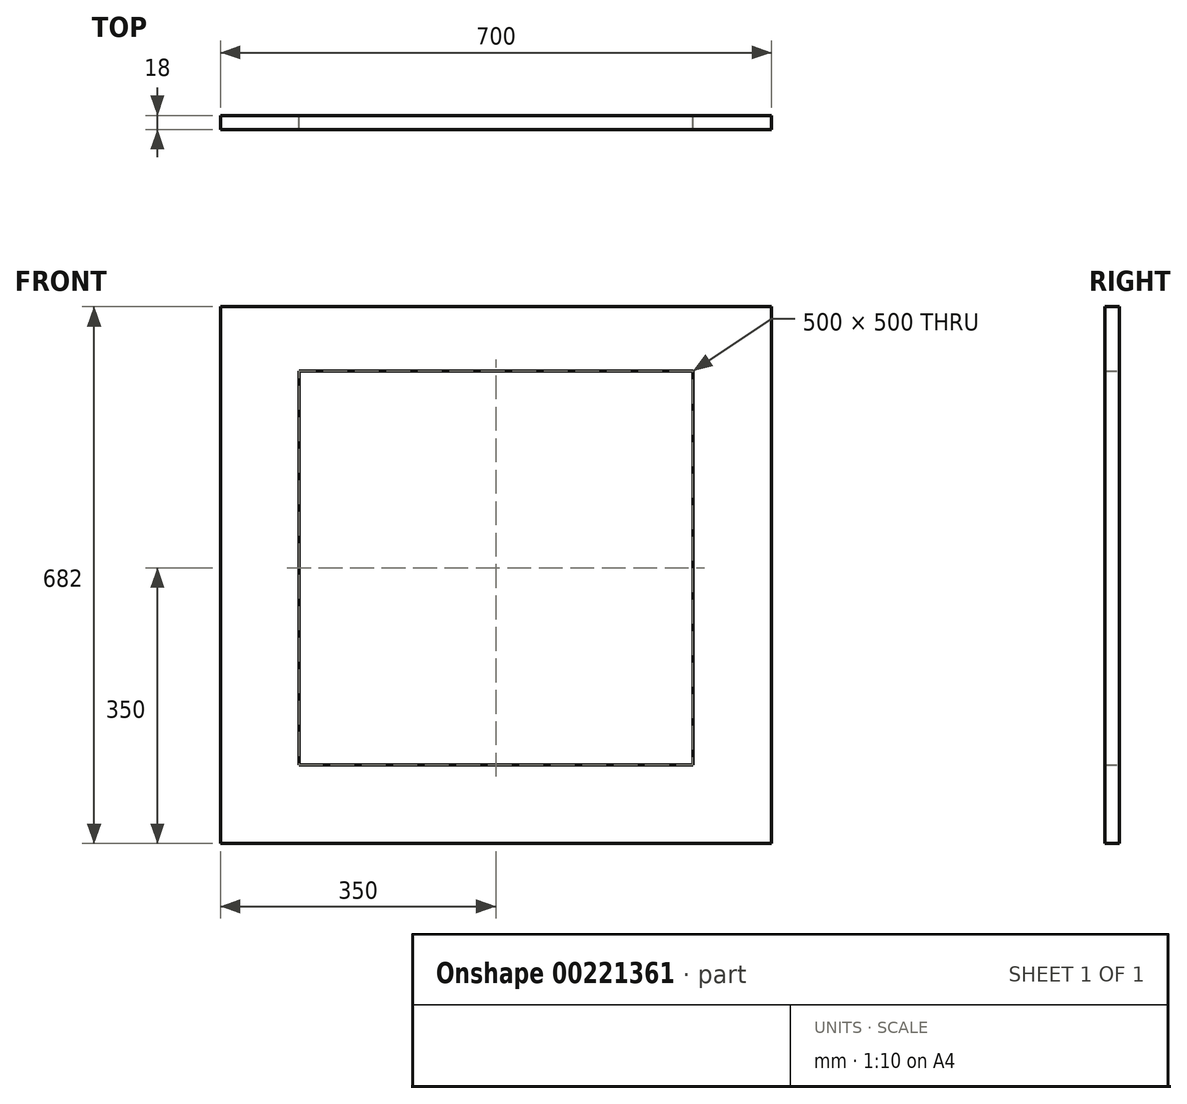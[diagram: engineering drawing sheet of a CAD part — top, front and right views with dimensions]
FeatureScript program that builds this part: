
annotation { "Feature Type Name" : "Feature", "Feature Type Description" : "" }
export const myFeature = defineFeature(function(context is Context, id is Id, definition is map)
    precondition{}
    {
        {
            var Q0;
            Q0=qCreatedBy(makeId("Front.planeOp"),FACE);
            var sketch = newSketch(context, id + "F0", { "sketchPlane" : qUnion([Q0])});
            skLineSegment(sketch, "E0.bottom", {"start": v(350, -341) * mm, "end": v(-350, -341) * mm});
            skLineSegment(sketch, "E0.top", {"start": v(350, 341) * mm, "end": v(-350, 341) * mm});
            skLineSegment(sketch, "E0.left", {"start": v(350, -341) * mm, "end": v(350, 341) * mm});
            skLineSegment(sketch, "E0.right", {"start": v(-350, -341) * mm, "end": v(-350, 341) * mm});
            skPoint(sketch, "E0.middle", {"position": v(0, 0) * mm});
            skLineSegment(sketch, "E1", {"start": v(-250, 259) * mm, "end": v(250, 259) * mm});
            skLineSegment(sketch, "E2", {"start": v(250, 259) * mm, "end": v(250, -241) * mm});
            skLineSegment(sketch, "E3", {"start": v(250, -241) * mm, "end": v(-250, -241) * mm});
            skLineSegment(sketch, "E4", {"start": v(-250, -241) * mm, "end": v(-250, 259) * mm});
            skSolve(sketch);
        }
        {
            var Q0;
            Q0 = qSketchRegion(id + "F0", true);
            extrude(context, id + "F1", {"entities" : qUnion([Q0]), "depth" : 18 * mm});
        }
    });
